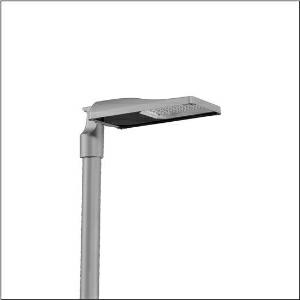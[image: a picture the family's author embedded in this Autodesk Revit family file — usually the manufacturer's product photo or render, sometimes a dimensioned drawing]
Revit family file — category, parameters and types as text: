
# Revit family: streetlight_sl_31_mini___st1_0a_5xh2d3ab08ja_f81c
name_source: partatom
category: Lighting Fixtures
units: mm (PartAtom-declared; Revit-internal decimal feet)

## family parameters
Cut with Voids When Loaded = No
Host = Face
Light Source = No
Part Type = Normal
Room Calculation Point = No
Round Connector Dimension = Use Diameter
Shared = No

## types (1)
- --- (1 x LED, 12140 lm, 81.1 W, 3000K)
    Apparent Load = 81 VA
    CIE Flux Codes = 40 73 97 100 100
    Color Rendering = 70
    Color Temperature = 3000K
    Default Elevation = 1800 mm
    Description = Streetlight SL 31 mini Easy LST mast luminaire for post-top, side-entry; light control with lens of PMMA; light distribution: ST1.0a, direct asymmetric distribution, for standard-compliant lighting for roads and squares; LED: luminous flux: 12.140lm, light colour: 730, colour temperature: 3000K; luminous efficacy: 149,7lm/W; control: pre-setting: linear dimming characteristic, flexible luminous flux parameterisation, time-dependent luminous flux control, constant luminous flux control, power reduction, intelligent temperature release in ECG and LED module, overheat protection; luminaire housing, of diecast aluminium, Siteco® metallic grey (DB 702S), corrosivity category C5 high according to DIN EN ISO 12944; cover of toughened safety glass, transparent, mast flange of diecast aluminium, Siteco® metallic grey (DB 702S), spigot size: 76/60mm, mast flange included unmounted; with cable H07RN-F 3x 1.5mm², cable length: 10,5m, connection cable pre-assembled; mains connection: 220..240V, AC, 50/60Hz; power consumption (at start of service life): 81,1W / (at end of service life): 88,3W / (with reduced operation 50%): 36,4W; protection rating (complete): IP66; insulation class (complete): insulation class II (safety insulation); impact resistance: IK10; certification: CE, ENEC, ENEC+, VDE, UKCA; permissible operating ambient temperature for outdoor applications: -40..+50°C; packaging unit: 1 piece

Light Distribution: ST1.0a
    Height = 76 mm
    Lamp = 1 x LED
    Lamp Light Flux = 12140 lm
    Lamp Power = 81.1 W
    Lamp count = 1
    Length = 547 mm
    Luminous efficacy = 150 lm/W
    Manufacturer = Siteco
    ModVariant = No
    Model = 5XH2D3AB08JA
    Number of Poles = 1
    OnlyDefault = Yes
    Power Factor = 1
    Product Name = Streetlight SL 31 mini | ST1.0a
    Product group = mast luminaire | pylon top
    ProductGroupID = 6100
    Protection Class = Protection class II
    Protection Degree = IP 66
    RLX_Detail_Level = 1
    RLX_Emergency_Light_Flux = 0 lm
    RLX_Emergency_Type = 0
    RLX_Emergency_Type_DB = No
    RlxData = <blob elided: 39601 chars, md5=f6569b9f>
    Socket = socket
    Standby Power = 0 W
    System Light Flux = 12140 lm
    System Power = 81 W
    Type Comments = factory setting: luminous flux: 100 % | dim-lin: 254 | 860 mA
    Type Image = l_1300326.jpg
    URL = http://relux.com
    VarID = @adj_051006
    Voltage = 0 V
    Weight = 0.00 kg
    Width = 265 mm

## geometry (parser evidence)
native form markers: Blend x4, Sweep x10
no freeform markers — native parametric forms only
